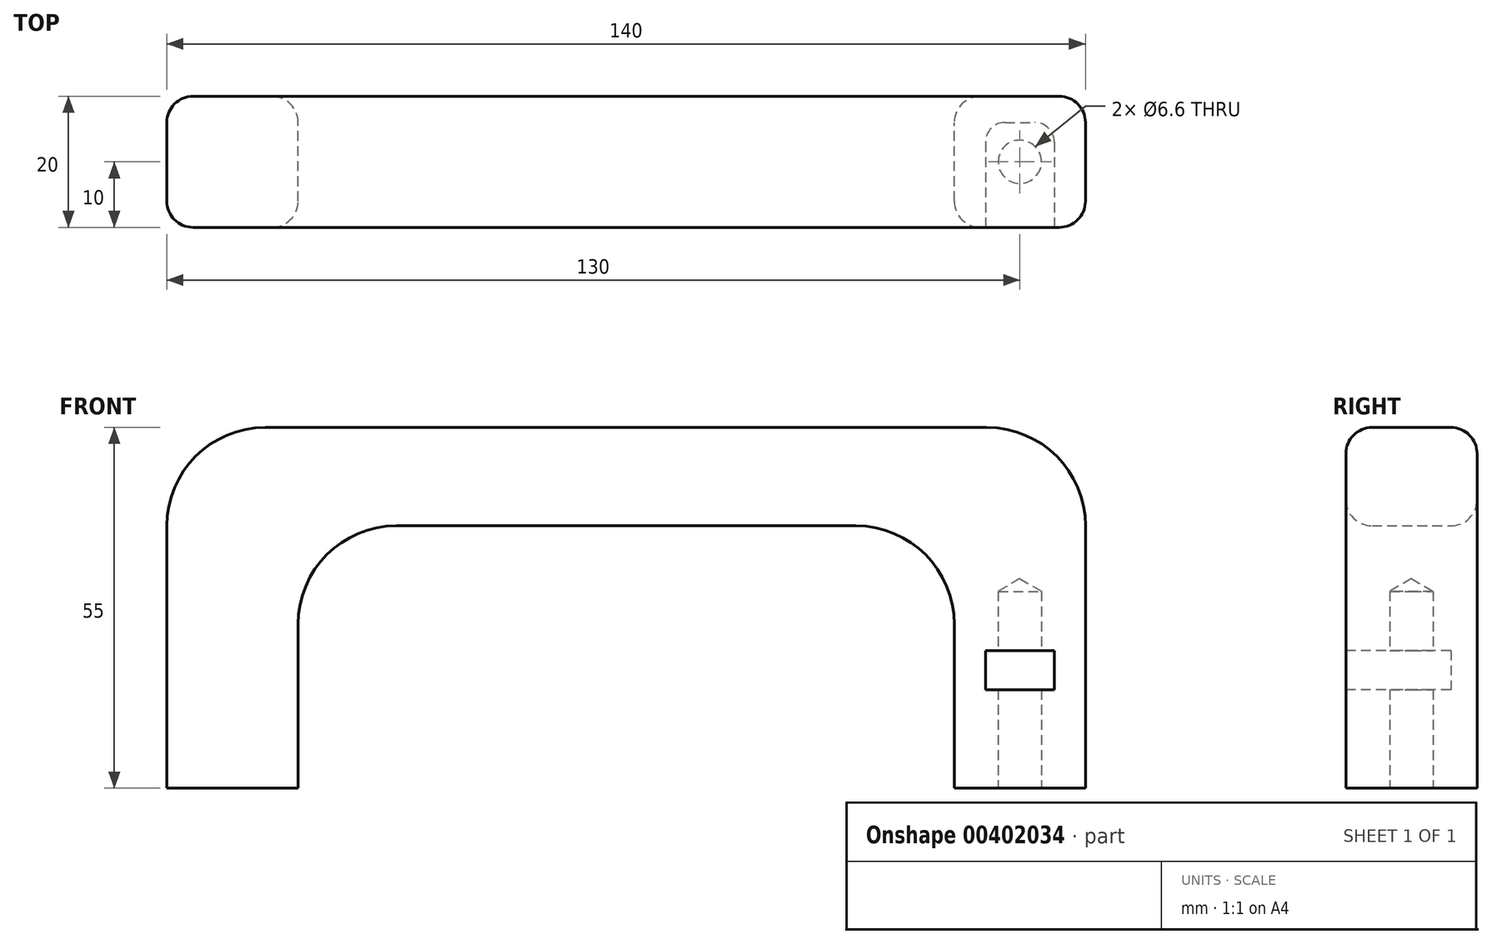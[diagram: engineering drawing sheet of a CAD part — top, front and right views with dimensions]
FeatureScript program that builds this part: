
annotation { "Feature Type Name" : "Feature", "Feature Type Description" : "" }
export const myFeature = defineFeature(function(context is Context, id is Id, definition is map)
    precondition{}
    {
        {
            var Q0;
            Q0=qCreatedBy(makeId("Front.planeOp"),FACE);
            var sketch = newSketch(context, id + "F0", { "sketchPlane" : qUnion([Q0])});
            skLineSegment(sketch, "E0", {"start": v(-70, 0) * mm, "end": v(-70, 55) * mm});
            skLineSegment(sketch, "E1", {"start": v(-70, 55) * mm, "end": v(70, 55) * mm});
            skLineSegment(sketch, "E2", {"start": v(70, 55) * mm, "end": v(70, 0) * mm});
            skLineSegment(sketch, "E3", {"start": v(70, 0) * mm, "end": v(50, 0) * mm});
            skLineSegment(sketch, "E4", {"start": v(50, 0) * mm, "end": v(50, 40) * mm});
            skLineSegment(sketch, "E5", {"start": v(50, 40) * mm, "end": v(-50, 40) * mm});
            skLineSegment(sketch, "E6", {"start": v(-50, 40) * mm, "end": v(-50, 0) * mm});
            skLineSegment(sketch, "E7", {"start": v(-50, 0) * mm, "end": v(-70, 0) * mm});
            skSolve(sketch);
        }
        {
            var Q0;
            Q0=makeQuery(id+"F0.imprint","IMPRINT",FACE,{"disambiguationData":[TD([[makeQuery(id+"F0.imprint","IMPRINT",EDGE,{"derivedFrom":sQuery(id+"F0.wireOp",EDGE,"E0")}),-1.0]])]});
            extrude(context, id + "F1", {"entities" : qUnion([Q0]), "endBound" : BoundingType.SYMMETRIC, "depth" : 20 * mm});
        }
        {
            var Q0;
            Q0=makeQuery(id+"F1.opExtrude","SWEPT_EDGE",EDGE,{"disambiguationData":[OSD([sQuery(id+"F0.wireOp",EDGE,"E0"),sQuery(id+"F0.wireOp",EDGE,"E1")])]});
            var Q1;
            Q1=makeQuery(id+"F1.opExtrude","SWEPT_EDGE",EDGE,{"disambiguationData":[OSD([sQuery(id+"F0.wireOp",EDGE,"E1"),sQuery(id+"F0.wireOp",EDGE,"E2")])]});
            var Q2;
            Q2=makeQuery(id+"F1.opExtrude","SWEPT_EDGE",EDGE,{"disambiguationData":[OSD([sQuery(id+"F0.wireOp",EDGE,"E4"),sQuery(id+"F0.wireOp",EDGE,"E5")])]});
            var Q3;
            Q3=makeQuery(id+"F1.opExtrude","SWEPT_EDGE",EDGE,{"disambiguationData":[OSD([sQuery(id+"F0.wireOp",EDGE,"E5"),sQuery(id+"F0.wireOp",EDGE,"E6")])]});
            fillet(context, id + "F2", {"entities" : qUnion([Q0, Q1, Q2, Q3]), "radius" : 15 * mm, "tangentPropagation" : true, "allowEdgeOverflow" : false});
        }
        {
            var Q0;
            Q0=makeQuery(id+"F1.opExtrude","CAP_FACE",FACE,{"disambiguationData":[OSD([sQuery(id+"F0.wireOp",EDGE,"E0"),sQuery(id+"F0.wireOp",EDGE,"E1"),sQuery(id+"F0.wireOp",EDGE,"E2"),sQuery(id+"F0.wireOp",EDGE,"E3"),sQuery(id+"F0.wireOp",EDGE,"E4"),sQuery(id+"F0.wireOp",EDGE,"E5"),sQuery(id+"F0.wireOp",EDGE,"E6"),sQuery(id+"F0.wireOp",EDGE,"E7")])],"isStart":false});
            var sketch = newSketch(context, id + "F3", { "sketchPlane" : qUnion([Q0])});
            skLineSegment(sketch, "E8.bottom", {"start": v(54.75, 21) * mm, "end": v(65.25, 21) * mm});
            skLineSegment(sketch, "E8.top", {"start": v(54.75, 15) * mm, "end": v(65.25, 15) * mm});
            skLineSegment(sketch, "E8.left", {"start": v(54.75, 21) * mm, "end": v(54.75, 15) * mm});
            skLineSegment(sketch, "E8.right", {"start": v(65.25, 21) * mm, "end": v(65.25, 15) * mm});
            skSolve(sketch);
        }
        {
            var Q0;
            Q0=makeQuery(id+"F3.imprint","IMPRINT",FACE,{"disambiguationData":[TD([[makeQuery(id+"F3.imprint","IMPRINT",EDGE,{"derivedFrom":sQuery(id+"F3.wireOp",EDGE,"E8.bottom")}),-1.0]])]});
            extrude(context, id + "F4", {"entities" : qUnion([Q0]), "operationType" : NewBodyOperationType.REMOVE, "oppositeDirection" : true, "depth" : 16 * mm});
        }
        {
            var Q0;
            Q0=makeQuery(id+"F1.opExtrude","SWEPT_FACE",FACE,{"disambiguationData":[OSD([sQuery(id+"F0.wireOp",EDGE,"E3")])]});
            var sketch = newSketch(context, id + "F5", { "sketchPlane" : qUnion([Q0])});
            skPoint(sketch, "E9", {"position": v(60, 0) * mm});
            skSolve(sketch);
        }
        {
            var Q0;
            Q0=sQuery(id+"F5.wireOp",VERTEX,"E9");
            var Q1;
            Q1=makeQuery(id+"F1.opExtrude","SWEPT_BODY",BODY,{"disambiguationData":[OSD([sQuery(id+"F0.wireOp",EDGE,"E0"),sQuery(id+"F0.wireOp",EDGE,"E1"),sQuery(id+"F0.wireOp",EDGE,"E2"),sQuery(id+"F0.wireOp",EDGE,"E3"),sQuery(id+"F0.wireOp",EDGE,"E4"),sQuery(id+"F0.wireOp",EDGE,"E5"),sQuery(id+"F0.wireOp",EDGE,"E6"),sQuery(id+"F0.wireOp",EDGE,"E7")])]});
            hole(context, id + "F6", {"style" : HoleStyle.SIMPLE, "endStyle" : HoleEndStyle.BLIND, "standardTappedOrClearance" : lookupTablePath({ "standard" : "ISO", "size" : "6.6", "type" : "Drilled" }), "standardBlindInLast" : lookupTablePath({ "standard" : "ISO", "size" : "6.6", "type" : "Drilled" }), "holeDiameter" : 6.6 * mm, "holeDepth" : 30 * mm, "isTappedThrough" : true, "tappedDepth" : 12 * mm, "tapClearance" : 3, "locations" : qUnion([Q0]), "scope" : qUnion([Q1])});
        }
        {
            var Q0;
            Q0=makeQuery(id+"F4.boolean.opBoolean","COPY",EDGE,{"derivedFrom":makeQuery(id+"F4.opExtrude","CAP_EDGE",EDGE,{"disambiguationData":[OSD([sQuery(id+"F3.wireOp",EDGE,"E8.left")])],"isStart":false})});
            var Q1;
            Q1=makeQuery(id+"F4.boolean.opBoolean","COPY",EDGE,{"derivedFrom":makeQuery(id+"F4.opExtrude","CAP_EDGE",EDGE,{"disambiguationData":[OSD([sQuery(id+"F3.wireOp",EDGE,"E8.right")])],"isStart":false})});
            fillet(context, id + "F7", {"entities" : qUnion([Q0, Q1]), "radius" : 3 * mm, "tangentPropagation" : true, "allowEdgeOverflow" : false});
        }
        {
            var Q0;
            Q0=makeQuery(id+"F1.opExtrude","CAP_EDGE",EDGE,{"disambiguationData":[OSD([sQuery(id+"F0.wireOp",EDGE,"E6")])],"isStart":false});
            var Q1;
            Q1=makeQuery(id+"F1.opExtrude","CAP_EDGE",EDGE,{"disambiguationData":[OSD([sQuery(id+"F0.wireOp",EDGE,"E6")])],"isStart":true});
            var Q2;
            Q2=makeQuery(id+"F1.opExtrude","CAP_EDGE",EDGE,{"disambiguationData":[OSD([sQuery(id+"F0.wireOp",EDGE,"E0")])],"isStart":true});
            var Q3;
            Q3=makeQuery(id+"F1.opExtrude","CAP_EDGE",EDGE,{"disambiguationData":[OSD([sQuery(id+"F0.wireOp",EDGE,"E0")])],"isStart":false});
            fillet(context, id + "F8", {"entities" : qUnion([Q0, Q1, Q2, Q3]), "radius" : 4 * mm, "tangentPropagation" : true, "allowEdgeOverflow" : false});
        }
    });
